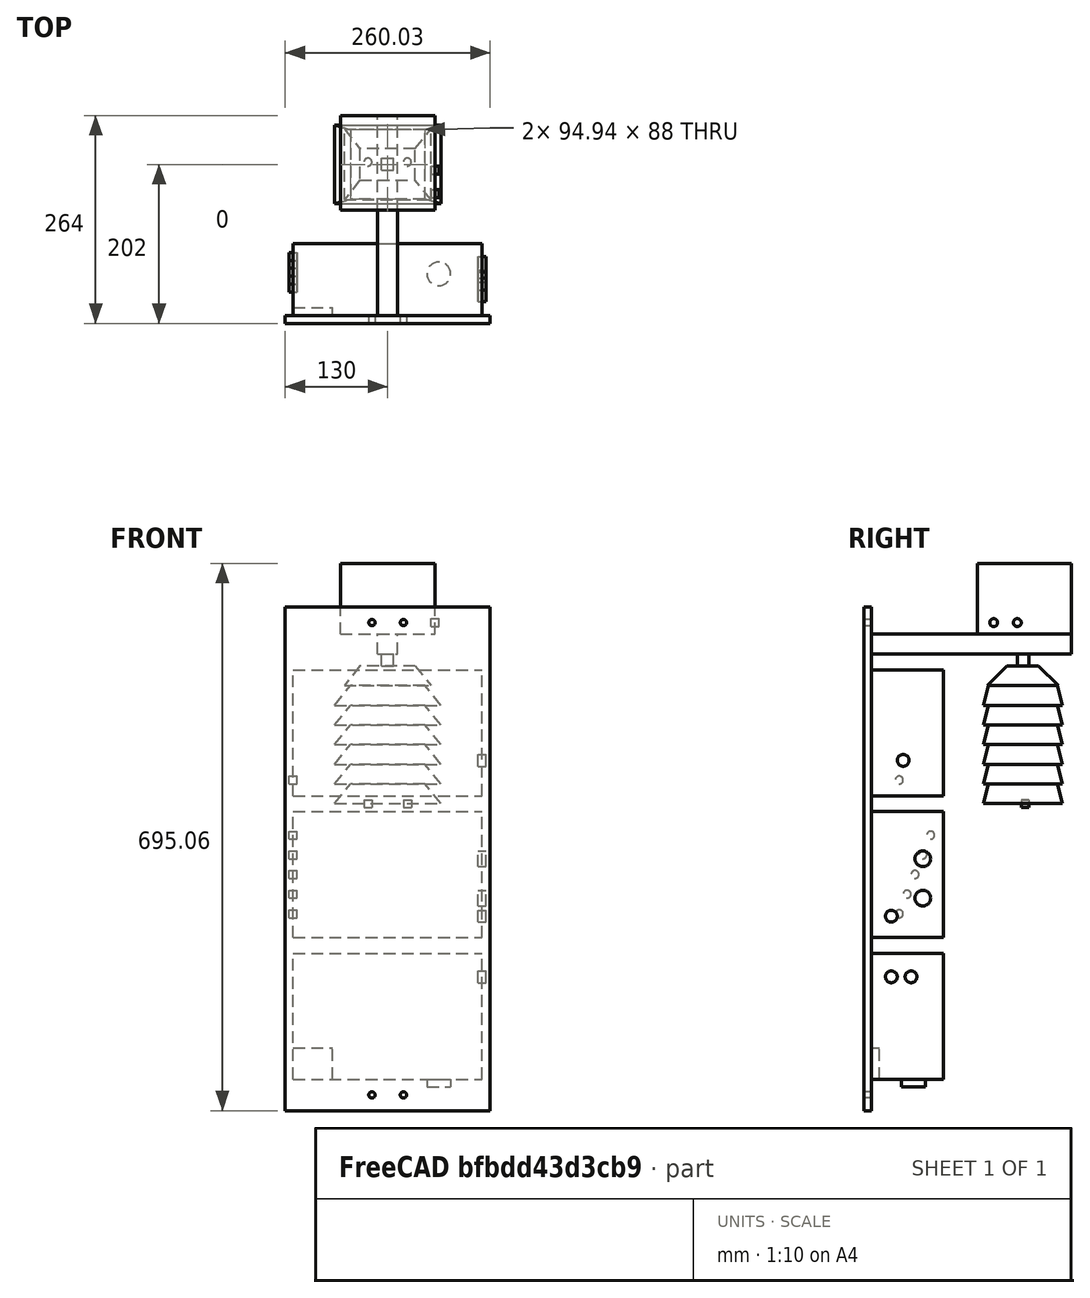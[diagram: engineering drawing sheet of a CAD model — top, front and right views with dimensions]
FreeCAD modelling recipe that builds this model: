
FCSTD DOCUMENT  (FreeCAD 0.17R13541 (Git))
Label: Latest2
License: All rights reserved
LicenseURL: http://en.wikipedia.org/wiki/All_rights_reserved
objects: Part::Box×38, Part::Cylinder×19, Part::Cut×16, Part::MultiCommon×10, Part::MultiFuse×3
note: 86 computed .brp shape members not serialized (recipe doc carries the construction recipe); baked Part::Feature solids carry a one-line shape summary decoded from their .brp

FEATURE [Part::Box] Box  label="Power Module "
  AttacherType = Attacher::AttachEngine3D
  Height = 160.02
  Length = 240.03
  Width = 91.44
FEATURE [Part::Box] Box001  label="Main Module"
  AttacherType = Attacher::AttachEngine3D
  Height = 160.02
  Length = 240.03
  Placement = pos=(0,0,180) rot=(0,0,1;0rad)
  Width = 91.44
FEATURE [Part::Box] Box002  label="Ozone Module"
  AttacherType = Attacher::AttachEngine3D
  Height = 160.02
  Length = 240.03
  Placement = pos=(0,0,360) rot=(0,0,1;0rad)
  Width = 91.44
FEATURE [Part::Box] Box003  label="Light Module"
  AttacherType = Attacher::AttachEngine3D
  Height = 89.66
  Length = 119.89
  Placement = pos=(60.05,134.1,565.4) rot=(0,0,1;0rad)
  Width = 119.89
FEATURE [Part::Box] Box005  label="Railing"
  AttacherType = Attacher::AttachEngine3D
  Height = 25.4
  Length = 25.4
  Placement = pos=(107.3,0,540) rot=(0,0,1;0rad)
  Width = 254
FEATURE [Part::Box] Box006  label="BackPanel"
  AttacherType = Attacher::AttachEngine3D
  Height = 640
  Length = 260.03
  Placement = pos=(-10,-10,-40) rot=(0,0,1;0rad)
  Width = 10
FEATURE [Part::Box] Box008  label="Cube001"
  AttacherType = Attacher::AttachEngine3D
  Height = 200
  Length = 200
  Placement = pos=(-22,-226,0) rot=(-1,0,0;0.235619rad)
  Width = 500
FEATURE [Part::Box] Box009  label="Acu1"
  AttacherType = Attacher::AttachEngine3D
  Height = 25
  Length = 135
  Placement = pos=(0,-226,0) rot=(0,0,1;0rad)
  Width = 100
FEATURE [Part::Box] Box010  label="Cube"
  AttacherType = Attacher::AttachEngine3D
  Height = 200
  Length = 20
  Placement = pos=(135,-236,0) rot=(0,-1,0;0.675442rad)
  Width = 500
FEATURE [Part::Box] Box011  label="Cube002"
  AttacherType = Attacher::AttachEngine3D
  Height = 500
  Length = 500
  Placement = pos=(0,-236,0) rot=(0,1,0;0.675442rad)
  Width = 500
FEATURE [Part::Cut] Cut
  Base = -> Box009
  Tool = -> Box010
FEATURE [Part::MultiCommon] Common
  Shapes = -> [Box011,Cut]
FEATURE [Part::MultiCommon] Common001
  Shapes = -> [Common,Box008]
FEATURE [Part::Box] Box012  label="Cube003"
  AttacherType = Attacher::AttachEngine3D
  Height = 88
  Length = 200
  Placement = pos=(-33,-126,0) rot=(1,0,0;0.235619rad)
  Width = 55
FEATURE [Part::Cut] Cut001  label="Enclosure Common000"
  Base = -> Common001
  Placement = pos=(52.5,368,475) rot=(0,0,1;0rad)
  Tool = -> Box012
FEATURE [Part::Box] Box013  label="Cube004"
  AttacherType = Attacher::AttachEngine3D
  Height = 25
  Length = 110
  Placement = pos=(311,-226,0) rot=(0,0,1;0rad)
  Width = 90
FEATURE [Part::Box] Box014  label="Cube005"
  AttacherType = Attacher::AttachEngine3D
  Height = 25
  Length = 110
  Placement = pos=(311,-226,0) rot=(1,0,0;0.785398rad)
  Width = 90
FEATURE [Part::Box] Box015  label="Cube006"
  AttacherType = Attacher::AttachEngine3D
  Height = 42
  Length = 110
  Placement = pos=(311,-136,0) rot=(1,0,0;0.785398rad)
  Width = 90
FEATURE [Part::Box] Box017  label="Cube008"
  AttacherType = Attacher::AttachEngine3D
  Height = 46
  Length = 110
  Placement = pos=(421,-226,0) rot=(0,-1,0;0.675442rad)
  Width = 120
FEATURE [Part::Cut] Cut002
  Base = -> Box013
  Tool = -> Box014
FEATURE [Part::Box] Box018  label="Cube009"
  AttacherType = Attacher::AttachEngine3D
  Height = 15
  Length = 15
  Placement = pos=(112.5,185,525) rot=(0,0,1;0rad)
  Width = 15
FEATURE [Part::Box] Box019  label="Acu002"
  AttacherType = Attacher::AttachEngine3D
  Height = 25
  Length = 135
  Placement = pos=(0,-226,0) rot=(0,0,1;0rad)
  Width = 100
FEATURE [Part::Box] Box020  label="Cube010"
  AttacherType = Attacher::AttachEngine3D
  Height = 200
  Length = 200
  Placement = pos=(-22,-226,0) rot=(-1,0,0;0.235619rad)
  Width = 500
FEATURE [Part::Box] Box021  label="Cube011"
  AttacherType = Attacher::AttachEngine3D
  Height = 500
  Length = 500
  Placement = pos=(0,-236,0) rot=(0,1,0;0.675442rad)
  Width = 500
FEATURE [Part::Box] Box022  label="Cube012"
  AttacherType = Attacher::AttachEngine3D
  Height = 200
  Length = 20
  Placement = pos=(135,-236,0) rot=(0,-1,0;0.675442rad)
  Width = 500
FEATURE [Part::Box] Box023  label="Cube013"
  AttacherType = Attacher::AttachEngine3D
  Height = 88
  Length = 200
  Placement = pos=(-33,-126,0) rot=(1,0,0;0.235619rad)
  Width = 55
FEATURE [Part::Cut] Cut007
  Base = -> Box019
  Tool = -> Box022
FEATURE [Part::MultiCommon] Common002
  Shapes = -> [Box021,Cut007]
FEATURE [Part::MultiCommon] Common003
  Shapes = -> [Common002,Box020]
FEATURE [Part::Cut] Cut006  label="Enclosure Common001"
  Base = -> Common003
  Placement = pos=(52.5,368,450) rot=(0,0,1;0rad)
  Tool = -> Box023
FEATURE [Part::Box] Box024  label="Acu003"
  AttacherType = Attacher::AttachEngine3D
  Height = 25
  Length = 135
  Placement = pos=(0,-226,0) rot=(0,0,1;0rad)
  Width = 100
FEATURE [Part::Box] Box025  label="Cube014"
  AttacherType = Attacher::AttachEngine3D
  Height = 200
  Length = 200
  Placement = pos=(-22,-226,0) rot=(-1,0,0;0.235619rad)
  Width = 500
FEATURE [Part::Box] Box026  label="Cube015"
  AttacherType = Attacher::AttachEngine3D
  Height = 88
  Length = 200
  Placement = pos=(-33,-126,0) rot=(1,0,0;0.235619rad)
  Width = 55
FEATURE [Part::Box] Box027  label="Cube016"
  AttacherType = Attacher::AttachEngine3D
  Height = 500
  Length = 500
  Placement = pos=(0,-236,0) rot=(0,1,0;0.675442rad)
  Width = 500
FEATURE [Part::Box] Box028  label="Cube017"
  AttacherType = Attacher::AttachEngine3D
  Height = 200
  Length = 20
  Placement = pos=(135,-236,0) rot=(0,-1,0;0.675442rad)
  Width = 500
FEATURE [Part::Cut] Cut008
  Base = -> Box024
  Tool = -> Box028
FEATURE [Part::MultiCommon] Common005
  Shapes = -> [Box027,Cut008]
FEATURE [Part::MultiCommon] Common004
  Shapes = -> [Common005,Box025]
FEATURE [Part::Cut] Cut009  label="Enclosure Common002"
  Base = -> Common004
  Placement = pos=(52.5,368,425) rot=(0,0,1;0rad)
  Tool = -> Box026
FEATURE [Part::Box] Box029  label="Acu004"
  AttacherType = Attacher::AttachEngine3D
  Height = 25
  Length = 135
  Placement = pos=(0,-226,0) rot=(0,0,1;0rad)
  Width = 100
FEATURE [Part::Box] Box030  label="Cube018"
  AttacherType = Attacher::AttachEngine3D
  Height = 200
  Length = 200
  Placement = pos=(-22,-226,0) rot=(-1,0,0;0.235619rad)
  Width = 500
FEATURE [Part::Box] Box031  label="Cube019"
  AttacherType = Attacher::AttachEngine3D
  Height = 88
  Length = 200
  Placement = pos=(-33,-126,0) rot=(1,0,0;0.235619rad)
  Width = 55
FEATURE [Part::Box] Box032  label="Cube020"
  AttacherType = Attacher::AttachEngine3D
  Height = 500
  Length = 500
  Placement = pos=(0,-236,0) rot=(0,1,0;0.675442rad)
  Width = 500
FEATURE [Part::Box] Box033  label="Cube021"
  AttacherType = Attacher::AttachEngine3D
  Height = 200
  Length = 20
  Placement = pos=(135,-236,0) rot=(0,-1,0;0.675442rad)
  Width = 500
FEATURE [Part::Cut] Cut010
  Base = -> Box029
  Tool = -> Box033
FEATURE [Part::MultiCommon] Common007
  Shapes = -> [Box032,Cut010]
FEATURE [Part::MultiCommon] Common006
  Shapes = -> [Common007,Box030]
FEATURE [Part::Cut] Cut011  label="Enclosure Common003"
  Base = -> Common006
  Placement = pos=(52.5,368,400) rot=(0,0,1;0rad)
  Tool = -> Box031
FEATURE [Part::Box] Box034  label="Acu005"
  AttacherType = Attacher::AttachEngine3D
  Height = 25
  Length = 135
  Placement = pos=(0,-226,0) rot=(0,0,1;0rad)
  Width = 100
FEATURE [Part::Box] Box035  label="Cube022"
  AttacherType = Attacher::AttachEngine3D
  Height = 200
  Length = 200
  Placement = pos=(-22,-226,0) rot=(-1,0,0;0.235619rad)
  Width = 500
FEATURE [Part::Box] Box036  label="Cube023"
  AttacherType = Attacher::AttachEngine3D
  Height = 88
  Length = 200
  Placement = pos=(-33,-126,0) rot=(1,0,0;0.235619rad)
  Width = 55
FEATURE [Part::Box] Box037  label="Cube024"
  AttacherType = Attacher::AttachEngine3D
  Height = 500
  Length = 500
  Placement = pos=(0,-236,0) rot=(0,1,0;0.675442rad)
  Width = 500
FEATURE [Part::Box] Box038  label="Cube025"
  AttacherType = Attacher::AttachEngine3D
  Height = 200
  Length = 20
  Placement = pos=(135,-236,0) rot=(0,-1,0;0.675442rad)
  Width = 500
FEATURE [Part::Cut] Cut012
  Base = -> Box034
  Tool = -> Box038
FEATURE [Part::MultiCommon] Common009
  Shapes = -> [Box037,Cut012]
FEATURE [Part::MultiCommon] Common008
  Shapes = -> [Common009,Box035]
FEATURE [Part::Cut] Cut013  label="Enclosure Common004"
  Base = -> Common008
  Placement = pos=(52.5,368,375) rot=(0,0,1;0rad)
  Tool = -> Box036
FEATURE [Part::Cut] Cut014  label="Enclosure Common005"
  Base = -> Common001
  Placement = pos=(52.5,368,350) rot=(0,0,1;0rad)
  Tool = -> Box012
FEATURE [Part::Cut] Cut003
  Base = -> Cut002
  Tool = -> Box015
FEATURE [Part::Box] Box016  label="Cube007"
  AttacherType = Attacher::AttachEngine3D
  Height = 25
  Length = 110
  Placement = pos=(311,-226,0) rot=(0,-1,0;0.912807rad)
  Width = 90
FEATURE [Part::Cut] Cut004
  Base = -> Cut003
  Tool = -> Box016
FEATURE [Part::Cut] Cut005  label="EnclousureTop"
  Base = -> Cut004
  Placement = pos=(-246,373,500) rot=(0,0,1;0rad)
  Tool = -> Box017
FEATURE [Part::Cylinder] Cylinder
  Angle = 360
  AttacherType = Attacher::AttachEngine3D
  Height = 10
  Placement = pos=(185,53,0) rot=(0,1,0;3.14159rad)
  Radius = 15
FEATURE [Part::Cylinder] Cylinder001  label="USB"
  Angle = 360
  AttacherType = Attacher::AttachEngine3D
  Height = 10
  Placement = pos=(235,65,230) rot=(0,1,0;1.5708rad)
  Radius = 10
FEATURE [Part::Cylinder] Cylinder002  label="HDMI"
  Angle = 360
  AttacherType = Attacher::AttachEngine3D
  Height = 10
  Placement = pos=(235,65,280) rot=(0,1,0;1.5708rad)
  Radius = 10
FEATURE [Part::Cylinder] Cylinder003  label="12V"
  Angle = 360
  AttacherType = Attacher::AttachEngine3D
  Height = 10
  Placement = pos=(235,50,130) rot=(0,1,0;1.5708rad)
  Radius = 7.5
FEATURE [Part::Cylinder] Cylinder004  label="5V"
  Angle = 360
  AttacherType = Attacher::AttachEngine3D
  Height = 10
  Placement = pos=(235,25,130) rot=(0,1,0;1.5708rad)
  Radius = 7.5
FEATURE [Part::Cylinder] Cylinder005  label="5V-2"
  Angle = 360
  AttacherType = Attacher::AttachEngine3D
  Height = 10
  Placement = pos=(235,25,207) rot=(0,1,0;1.5708rad)
  Radius = 7.5
FEATURE [Part::Cylinder] Cylinder006  label="12V-2"
  Angle = 360
  AttacherType = Attacher::AttachEngine3D
  Height = 10
  Placement = pos=(235,40,405) rot=(0,1,0;1.5708rad)
  Radius = 7.5
FEATURE [Part::Cylinder] Cylinder007  label="LightModuleUsb"
  Angle = 360
  AttacherType = Attacher::AttachEngine3D
  Height = 10
  Placement = pos=(-5,75,310) rot=(0,1,0;1.5708rad)
  Radius = 5
FEATURE [Part::Cylinder] Cylinder008  label="AirModuleUsb"
  Angle = 360
  AttacherType = Attacher::AttachEngine3D
  Height = 10
  Placement = pos=(-5,55,260) rot=(0,1,0;1.5708rad)
  Radius = 5
FEATURE [Part::Cylinder] Cylinder009  label="MicUsb"
  Angle = 360
  AttacherType = Attacher::AttachEngine3D
  Height = 10
  Placement = pos=(-5,45,235) rot=(0,1,0;1.5708rad)
  Radius = 5
FEATURE [Part::Cylinder] Cylinder010  label="OzoneUsb"
  Angle = 360
  AttacherType = Attacher::AttachEngine3D
  Height = 10
  Placement = pos=(-5,35,210) rot=(0,1,0;1.5708rad)
  Radius = 5
FEATURE [Part::Cylinder] Cylinder011  label="CameraUSB"
  Angle = 360
  AttacherType = Attacher::AttachEngine3D
  Height = 10
  Placement = pos=(-5,65,285) rot=(0,1,0;1.5708rad)
  Radius = 5
FEATURE [Part::Cylinder] Cylinder012  label="OzoneUsb-2"
  Angle = 360
  AttacherType = Attacher::AttachEngine3D
  Height = 10
  Placement = pos=(-5,35,380) rot=(0,1,0;1.5708rad)
  Radius = 5
FEATURE [Part::Cylinder] Cylinder013  label="LightModuleUsb-2"
  Angle = 360
  AttacherType = Attacher::AttachEngine3D
  Height = 10
  Placement = pos=(175,155,580) rot=(0,1,0;1.5708rad)
  Radius = 5
FEATURE [Part::Cylinder] Cylinder014  label="CameraUsb-2"
  Angle = 360
  AttacherType = Attacher::AttachEngine3D
  Height = 10
  Placement = pos=(175,185,580) rot=(0,1,0;1.5708rad)
  Radius = 5
FEATURE [Part::Cylinder] Cylinder015  label="MicUsb-2"
  Angle = 360
  AttacherType = Attacher::AttachEngine3D
  Height = 10
  Placement = pos=(145,195,355) rot=(0,1,0;3.14159rad)
  Radius = 5
FEATURE [Part::Cylinder] Cylinder016  label="AirUsb-2"
  Angle = 360
  AttacherType = Attacher::AttachEngine3D
  Height = 10
  Placement = pos=(95,195,355) rot=(0,1,0;3.14159rad)
  Radius = 5
FEATURE [Part::Cylinder] Cylinder017  label="CutOut"
  Angle = 360
  AttacherType = Attacher::AttachEngine3D
  Height = 10
  Placement = pos=(140,0,-20) rot=(1,0,0;1.5708rad)
  Radius = 4
FEATURE [Part::Cylinder] Cylinder018  label="CutOut001"
  Angle = 360
  AttacherType = Attacher::AttachEngine3D
  Height = 10
  Placement = pos=(100,0,-20) rot=(1,0,0;1.5708rad)
  Radius = 4
FEATURE [Part::MultiFuse] Fusion  label="Cutout1"
  Shapes = -> [Cylinder017,Cylinder018]
FEATURE [Part::MultiFuse] Fusion001
  Shapes = -> [Cut006,Cut009,Cut011,Cut013,Cut014,Cut001]
FEATURE [Part::MultiFuse] Fusion002  label="Cutout2"
  Placement = pos=(0,0,600) rot=(0,0,1;0rad)
  Shapes = -> [Cylinder017,Cylinder018]
FEATURE [Part::Cut] Cut015
  Base = -> Box006
  Tool = -> Fusion
FEATURE [Part::Box] Box039  label="Dispay"
  AttacherType = Attacher::AttachEngine3D
  Height = 40
  Length = 50
  Width = 10
